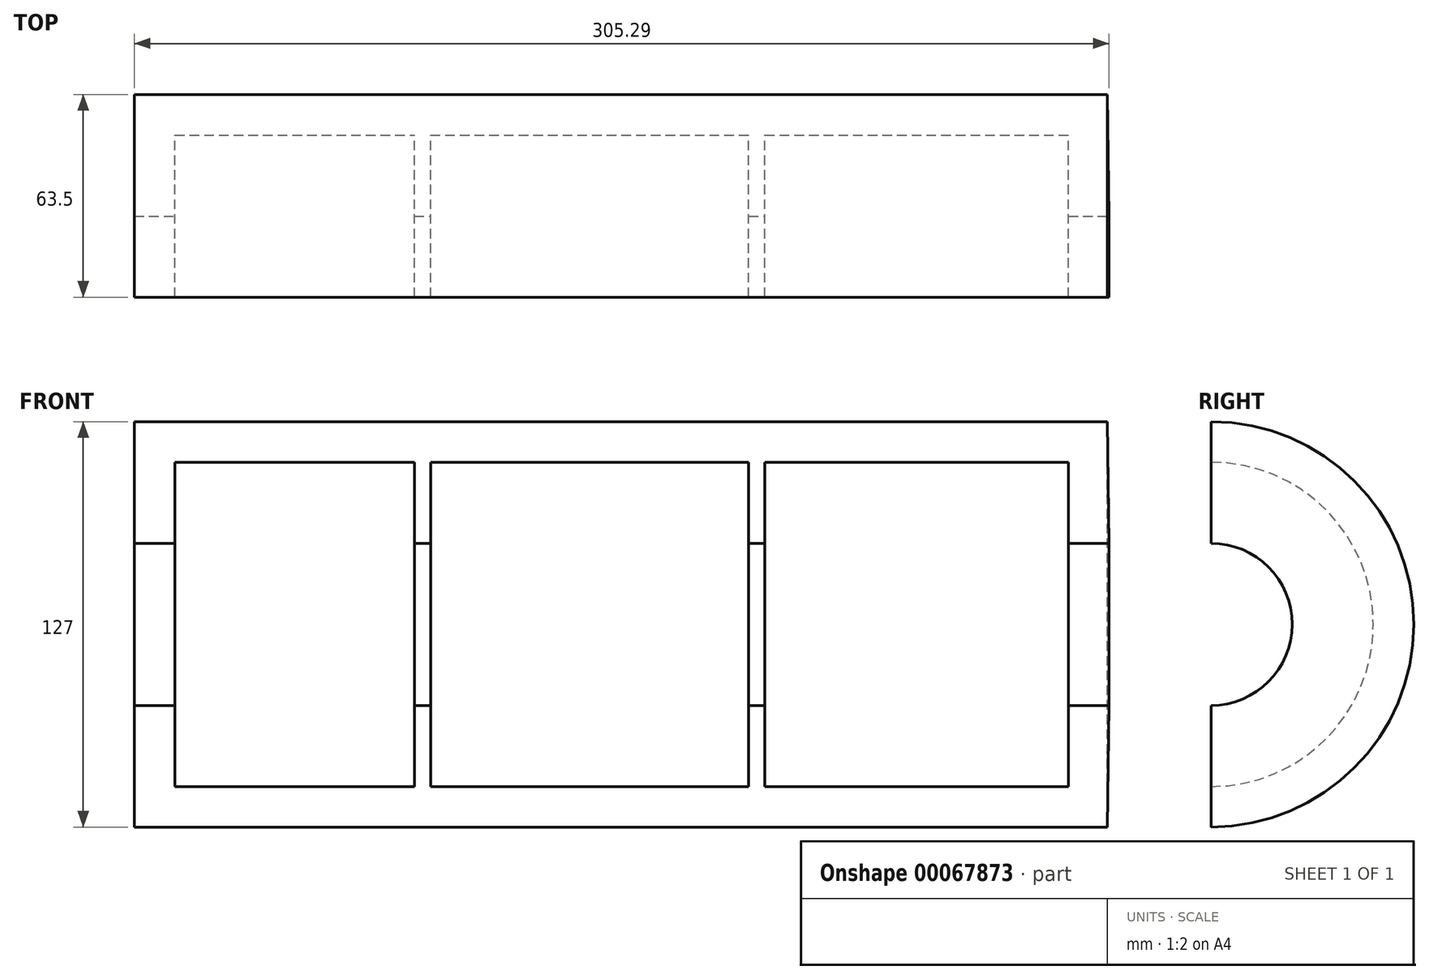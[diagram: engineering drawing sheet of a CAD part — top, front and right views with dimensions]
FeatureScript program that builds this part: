
annotation { "Feature Type Name" : "Feature", "Feature Type Description" : "" }
export const myFeature = defineFeature(function(context is Context, id is Id, definition is map)
    precondition{}
    {
        {
            var Q0;
            Q0=qCreatedBy(makeId("Front.planeOp"),FACE);
            var sketch = newSketch(context, id + "F0", { "sketchPlane" : qUnion([Q0])});
            skLineSegment(sketch, "E0", {"start": v(-152.15, 63.5) * mm, "end": v(152.65, 63.5) * mm});
            skLineSegment(sketch, "E1", {"start": v(-152.15, 63.5) * mm, "end": v(-152.15, 25.4) * mm});
            skLineSegment(sketch, "E2", {"start": v(-139.45, 50.8) * mm, "end": v(-64.46, 50.8) * mm});
            skLineSegment(sketch, "E3", {"start": v(-139.45, 50.8) * mm, "end": v(-139.45, 25.4) * mm});
            skLineSegment(sketch, "E4", {"start": v(-64.46, 50.8) * mm, "end": v(-64.46, 25.4) * mm});
            skLineSegment(sketch, "E5", {"start": v(-64.46, 25.4) * mm, "end": v(-59.38, 25.4) * mm});
            skLineSegment(sketch, "E6", {"start": v(-59.38, 25.4) * mm, "end": v(-59.38, 50.8) * mm});
            skLineSegment(sketch, "E7", {"start": v(-152.15, 25.4) * mm, "end": v(-139.45, 25.4) * mm});
            skLineSegment(sketch, "E8", {"start": v(153.14, 25.4) * mm, "end": v(140.44, 25.4) * mm});
            skLineSegment(sketch, "E9", {"start": v(140.44, 25.4) * mm, "end": v(140.44, 50.8) * mm});
            skLineSegment(sketch, "E10", {"start": v(40.3, 50.8) * mm, "end": v(40.3, 25.4) * mm});
            skLineSegment(sketch, "E11", {"start": v(40.3, 25.4) * mm, "end": v(45.38, 25.4) * mm});
            skLineSegment(sketch, "E12", {"start": v(45.38, 25.4) * mm, "end": v(45.38, 50.8) * mm});
            skLineSegment(sketch, "E13.trimOffspring", {"start": v(-59.38, 50.8) * mm, "end": v(40.3, 50.8) * mm});
            skLineSegment(sketch, "E14", {"start": v(189.4, 0) * mm, "end": v(-147.7, 0) * mm, "construction": true});
            skLineSegment(sketch, "E15", {"start": v(45.38, 50.8) * mm, "end": v(140.44, 50.8) * mm});
            skLineSegment(sketch, "E16", {"start": v(152.65, 63.5) * mm, "end": v(153.14, 25.4) * mm});
            skSolve(sketch);
        }
        {
            var Q0;
            Q0=makeQuery(id+"F0.imprint","IMPRINT",FACE,{"disambiguationData":[TD([[makeQuery(id+"F0.imprint","IMPRINT",EDGE,{"derivedFrom":sQuery(id+"F0.wireOp",EDGE,"E0")}),-1.0]])]});
            var Q1;
            Q1=sQuery(id+"F0.wireOp",EDGE,"E14");
            revolve(context, id + "F1", {"entities" : qUnion([Q0]), "axis" : qUnion([Q1]), "revolveType" : RevolveType.ONE_DIRECTION, "angle" : 180 * degree});
        }
    });
